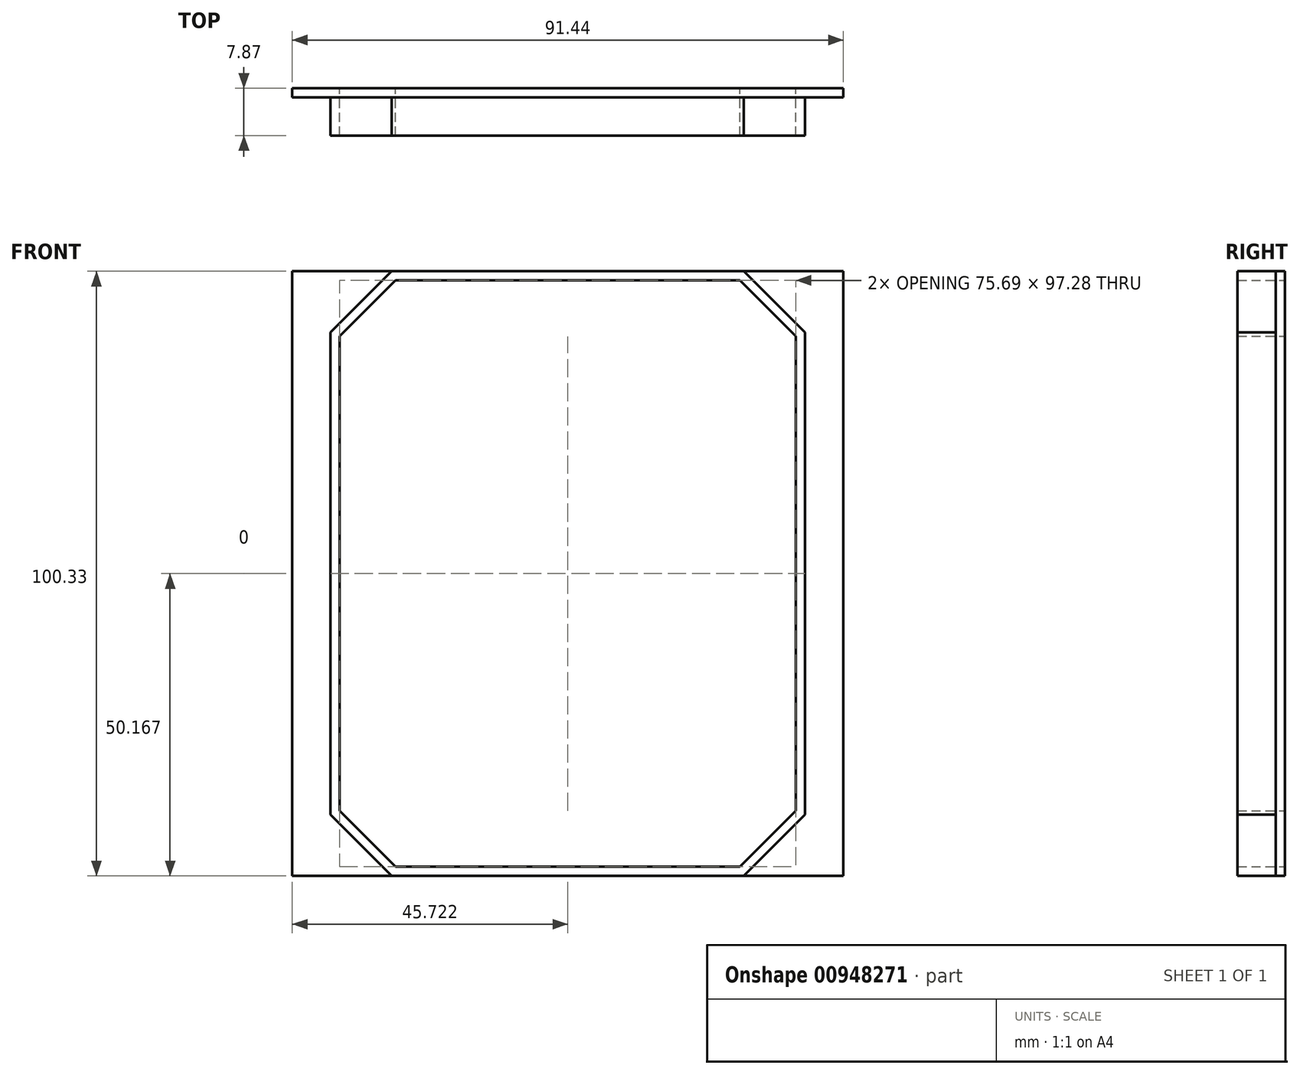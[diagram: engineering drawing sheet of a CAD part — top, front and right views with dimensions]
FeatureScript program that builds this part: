
annotation { "Feature Type Name" : "Feature", "Feature Type Description" : "" }
export const myFeature = defineFeature(function(context is Context, id is Id, definition is map)
    precondition{}
    {
        {
            var Q0;
            Q0=qCreatedBy(makeId("Front.planeOp"),FACE);
            var sketch = newSketch(context, id + "F0", { "sketchPlane" : qUnion([Q0])});
            skLineSegment(sketch, "E0.bottom", {"start": v(-45.92, 76.2) * mm, "end": v(12.5, 76.2) * mm});
            skLineSegment(sketch, "E0.top", {"start": v(-45.92, -24.14) * mm, "end": v(12.5, -24.14) * mm});
            skLineSegment(sketch, "E0.left", {"start": v(-56.08, 66.03) * mm, "end": v(-56.08, -13.98) * mm});
            skLineSegment(sketch, "E0.right", {"start": v(22.66, 66.03) * mm, "end": v(22.66, -13.98) * mm});
            skPoint(sketch, "E1.visualSharp", {"position": v(-47.73, 74.67) * mm});
            skPoint(sketch, "E2.visualSharp", {"position": v(27.96, -22.61) * mm});
            skPoint(sketch, "E3.visualSharp", {"position": v(-47.73, -22.61) * mm});
            skPoint(sketch, "E4.visualSharp", {"position": v(27.96, 74.67) * mm});
            skPoint(sketch, "E5.visualSharp", {"position": v(-56.08, 76.2) * mm});
            skPoint(sketch, "E6.visualSharp", {"position": v(22.66, 76.2) * mm});
            skPoint(sketch, "E7.visualSharp", {"position": v(22.66, -24.14) * mm});
            skPoint(sketch, "E8.visualSharp", {"position": v(-56.08, -24.14) * mm});
            skLineSegment(sketch, "E9", {"start": v(12.5, 76.2) * mm, "end": v(22.66, 66.03) * mm});
            skLineSegment(sketch, "E10", {"start": v(-45.92, 76.2) * mm, "end": v(-56.08, 66.03) * mm});
            skLineSegment(sketch, "E11", {"start": v(22.66, -13.98) * mm, "end": v(12.5, -24.14) * mm});
            skLineSegment(sketch, "E12", {"start": v(-45.92, -24.14) * mm, "end": v(-56.08, -13.98) * mm});
            skLineSegment(sketch, "E13.0", {"start": v(-45.29, 74.67) * mm, "end": v(11.87, 74.67) * mm});
            skLineSegment(sketch, "E13.1", {"start": v(-45.29, 74.67) * mm, "end": v(-54.55, 65.4) * mm});
            skLineSegment(sketch, "E13.2", {"start": v(11.87, 74.67) * mm, "end": v(21.14, 65.4) * mm});
            skLineSegment(sketch, "E13.3", {"start": v(-54.55, 65.4) * mm, "end": v(-54.55, -13.35) * mm});
            skLineSegment(sketch, "E13.4", {"start": v(21.14, 65.4) * mm, "end": v(21.14, -13.35) * mm});
            skLineSegment(sketch, "E13.5", {"start": v(21.14, -13.35) * mm, "end": v(11.87, -22.61) * mm});
            skLineSegment(sketch, "E13.6", {"start": v(-45.29, -22.61) * mm, "end": v(11.87, -22.61) * mm});
            skLineSegment(sketch, "E13.7", {"start": v(-45.29, -22.61) * mm, "end": v(-54.55, -13.35) * mm});
            skSolve(sketch);
        }
        {
            var Q0;
            Q0 = qSketchRegion(id + "F0", true);
            extrude(context, id + "F1", {"entities" : qUnion([Q0]), "depth" : 6.35 * mm, "offsetDistance" : 25.4 * mm});
        }
        {
            var Q0;
            Q0=makeQuery(id+"F1.opExtrude","CAP_FACE",FACE,{"disambiguationData":[OSD([sQuery(id+"F0.wireOp",EDGE,"E0.bottom"),sQuery(id+"F0.wireOp",EDGE,"E0.top"),sQuery(id+"F0.wireOp",EDGE,"E0.left"),sQuery(id+"F0.wireOp",EDGE,"E0.right"),sQuery(id+"F0.wireOp",EDGE,"E9"),sQuery(id+"F0.wireOp",EDGE,"E10"),sQuery(id+"F0.wireOp",EDGE,"E11"),sQuery(id+"F0.wireOp",EDGE,"E12"),sQuery(id+"F0.wireOp",EDGE,"E13.0"),sQuery(id+"F0.wireOp",EDGE,"E13.1"),sQuery(id+"F0.wireOp",EDGE,"E13.2"),sQuery(id+"F0.wireOp",EDGE,"E13.3"),sQuery(id+"F0.wireOp",EDGE,"E13.4"),sQuery(id+"F0.wireOp",EDGE,"E13.5"),sQuery(id+"F0.wireOp",EDGE,"E13.6"),sQuery(id+"F0.wireOp",EDGE,"E13.7")])],"isStart":true});
            var sketch = newSketch(context, id + "F2", { "sketchPlane" : qUnion([Q0])});
            skLineSegment(sketch, "E14.bottom", {"start": v(-29.01, 76.2) * mm, "end": v(62.43, 76.2) * mm});
            skLineSegment(sketch, "E14.top", {"start": v(-29.01, -24.14) * mm, "end": v(62.43, -24.14) * mm});
            skLineSegment(sketch, "E14.left", {"start": v(-29.01, 76.2) * mm, "end": v(-29.01, -24.14) * mm});
            skLineSegment(sketch, "E14.right", {"start": v(62.43, 76.2) * mm, "end": v(62.43, -24.14) * mm});
            skSolve(sketch);
        }
        {
            var Q0;
            Q0 = qSketchRegion(id + "F2", true);
            extrude(context, id + "F3", {"entities" : qUnion([Q0]), "operationType" : NewBodyOperationType.ADD, "depth" : 1.52 * mm, "offsetDistance" : 25.4 * mm});
        }
        {
            var Q0;
            Q0=makeQuery(id+"F3.boolean.opBoolean","SPLIT",FACE,{"disambiguationData":[TD([makeQuery(id+"F1.opExtrude","SWEPT_FACE",FACE,{"disambiguationData":[OSD([sQuery(id+"F0.wireOp",EDGE,"E13.0")])]})])],"derivedFrom":makeQuery(id+"F3.opExtrude","CAP_FACE",FACE,{"disambiguationData":[OSD([sQuery(id+"F2.wireOp",EDGE,"E14.bottom"),sQuery(id+"F2.wireOp",EDGE,"E14.top"),sQuery(id+"F2.wireOp",EDGE,"E14.left"),sQuery(id+"F2.wireOp",EDGE,"E14.right")])],"isStart":true})});
            var sketch = newSketch(context, id + "F4", { "sketchPlane" : qUnion([Q0])});
            skLineSegment(sketch, "E15", {"start": v(-45.29, 74.67) * mm, "end": v(-54.55, 65.4) * mm});
            skLineSegment(sketch, "E16", {"start": v(-54.55, 65.4) * mm, "end": v(-54.55, -13.35) * mm});
            skLineSegment(sketch, "E17", {"start": v(-54.55, -13.35) * mm, "end": v(-45.29, -22.61) * mm});
            skLineSegment(sketch, "E18", {"start": v(-45.29, -22.61) * mm, "end": v(11.87, -22.61) * mm});
            skLineSegment(sketch, "E19", {"start": v(11.87, -22.61) * mm, "end": v(21.14, -13.35) * mm});
            skLineSegment(sketch, "E20", {"start": v(21.14, -13.35) * mm, "end": v(21.14, 65.4) * mm});
            skLineSegment(sketch, "E21", {"start": v(21.14, 65.4) * mm, "end": v(11.87, 74.67) * mm});
            skLineSegment(sketch, "E22", {"start": v(11.87, 74.67) * mm, "end": v(-45.29, 74.67) * mm});
            skSolve(sketch);
        }
        {
            var Q0;
            Q0 = qSketchRegion(id + "F4", true);
            extrude(context, id + "F5", {"entities" : qUnion([Q0]), "operationType" : NewBodyOperationType.REMOVE, "endBound" : BoundingType.SYMMETRIC, "depth" : 10.67 * mm, "offsetDistance" : 25.4 * mm});
        }
        {
            var Q0;
            Q0 = qSketchRegion(id + "F0", true);
            extrude(context, id + "F6", {"entities" : qUnion([Q0]), "depth" : 6.35 * mm, "offsetDistance" : 25.4 * mm});
        }
    });
